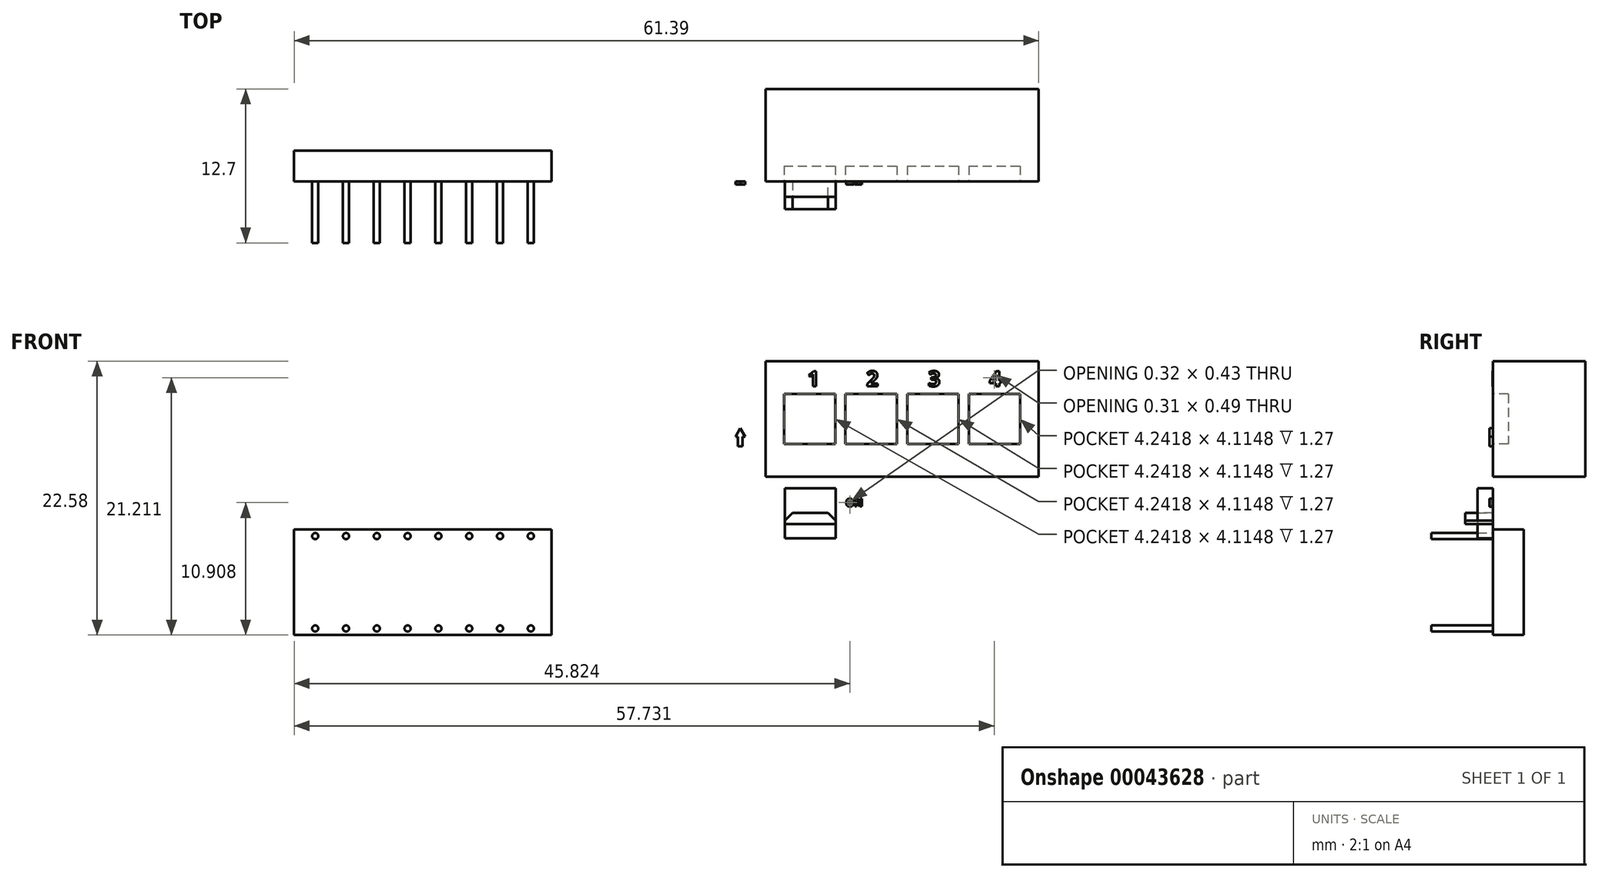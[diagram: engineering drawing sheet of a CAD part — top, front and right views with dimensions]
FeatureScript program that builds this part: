
annotation { "Feature Type Name" : "Feature", "Feature Type Description" : "" }
export const myFeature = defineFeature(function(context is Context, id is Id, definition is map)
    precondition{}
    {
        {
            var Q0;
            Q0=qCreatedBy(makeId("Front.planeOp"),FACE);
            var sketch = newSketch(context, id + "F0", { "sketchPlane" : qUnion([Q0])});
            skLineSegment(sketch, "E0.bottom", {"start": v(-10.98, 4.78) * mm, "end": v(11.55, 4.78) * mm});
            skLineSegment(sketch, "E0.top", {"start": v(-10.98, -4.77) * mm, "end": v(11.55, -4.77) * mm});
            skLineSegment(sketch, "E0.left", {"start": v(-10.98, 4.78) * mm, "end": v(-10.98, -4.77) * mm});
            skLineSegment(sketch, "E0.right", {"start": v(11.55, 4.78) * mm, "end": v(11.55, -4.77) * mm});
            skSolve(sketch);
        }
        {
            var Q0;
            Q0 = qSketchRegion(id + "F0", true);
            extrude(context, id + "F1", {"entities" : qUnion([Q0]), "oppositeDirection" : true, "depth" : 7.62 * mm});
        }
        {
            var Q0;
            Q0=qCreatedBy(makeId("Front.planeOp"),FACE);
            var sketch = newSketch(context, id + "F2", { "sketchPlane" : qUnion([Q0])});
            skLineSegment(sketch, "E1.bottom", {"start": v(-9.45, 2.07) * mm, "end": v(-5.21, 2.07) * mm});
            skLineSegment(sketch, "E1.top", {"start": v(-9.45, -2.05) * mm, "end": v(-5.21, -2.05) * mm});
            skLineSegment(sketch, "E1.left", {"start": v(-9.45, 2.07) * mm, "end": v(-9.45, -2.05) * mm});
            skLineSegment(sketch, "E1.right", {"start": v(-5.21, 2.07) * mm, "end": v(-5.21, -2.05) * mm});
            skLineSegment(sketch, "E2.bottom", {"start": v(-4.37, 2.07) * mm, "end": v(-0.13, 2.07) * mm});
            skLineSegment(sketch, "E2.left", {"start": v(-4.37, 2.07) * mm, "end": v(-4.37, -2.05) * mm});
            skLineSegment(sketch, "E2.top", {"start": v(-4.37, -2.05) * mm, "end": v(-0.13, -2.05) * mm});
            skLineSegment(sketch, "E2.right", {"start": v(-0.13, 2.07) * mm, "end": v(-0.13, -2.05) * mm});
            skLineSegment(sketch, "E3.bottom", {"start": v(0.7, 2.07) * mm, "end": v(4.95, 2.07) * mm});
            skLineSegment(sketch, "E3.left", {"start": v(0.7, 2.07) * mm, "end": v(0.7, -2.05) * mm});
            skLineSegment(sketch, "E3.top", {"start": v(0.7, -2.05) * mm, "end": v(4.95, -2.05) * mm});
            skLineSegment(sketch, "E3.right", {"start": v(4.95, 2.07) * mm, "end": v(4.95, -2.05) * mm});
            skLineSegment(sketch, "E4.bottom", {"start": v(5.79, 2.07) * mm, "end": v(10.03, 2.07) * mm});
            skLineSegment(sketch, "E4.left", {"start": v(5.79, 2.07) * mm, "end": v(5.79, -2.05) * mm});
            skLineSegment(sketch, "E4.top", {"start": v(5.79, -2.05) * mm, "end": v(10.03, -2.05) * mm});
            skLineSegment(sketch, "E4.right", {"start": v(10.03, 2.07) * mm, "end": v(10.03, -2.05) * mm});
            skSolve(sketch);
        }
        {
            var Q0;
            Q0 = qSketchRegion(id + "F2", true);
            extrude(context, id + "F3", {"entities" : qUnion([Q0]), "operationType" : NewBodyOperationType.REMOVE, "oppositeDirection" : true, "depth" : 1.27 * mm});
        }
        {
            var Q0;
            Q0=qCreatedBy(makeId("Front.planeOp"),FACE);
            var sketch = newSketch(context, id + "F4", { "sketchPlane" : qUnion([Q0])});
            skLineSegment(sketch, "E5.bottom", {"start": v(-9.38, -5.7) * mm, "end": v(-5.2, -5.7) * mm});
            skLineSegment(sketch, "E5.top", {"start": v(-9.38, -9.83) * mm, "end": v(-5.2, -9.83) * mm});
            skLineSegment(sketch, "E5.left", {"start": v(-9.38, -5.7) * mm, "end": v(-9.38, -9.83) * mm});
            skLineSegment(sketch, "E5.right", {"start": v(-5.2, -5.7) * mm, "end": v(-5.2, -9.83) * mm});
            skSolve(sketch);
        }
        {
            var Q0;
            Q0 = qSketchRegion(id + "F4", true);
            extrude(context, id + "F5", {"entities" : qUnion([Q0]), "depth" : 1.27 * mm});
        }
        {
            var Q0;
            Q0=qCreatedBy(makeId("Front.planeOp"),FACE);
            var sketch = newSketch(context, id + "F6", { "sketchPlane" : qUnion([Q0])});
            skLineSegment(sketch, "E6.bottom", {"start": v(-9.37, -8.66) * mm, "end": v(-5.19, -8.66) * mm});
            skLineSegment(sketch, "E6.top", {"start": v(-9.37, -7.72) * mm, "end": v(-5.19, -7.72) * mm});
            skLineSegment(sketch, "E6.left", {"start": v(-9.37, -8.66) * mm, "end": v(-9.37, -7.72) * mm});
            skLineSegment(sketch, "E6.right", {"start": v(-5.19, -8.66) * mm, "end": v(-5.19, -7.72) * mm});
            skSolve(sketch);
        }
        {
            var Q0;
            Q0 = qSketchRegion(id + "F6", true);
            var Q1;
            Q1=makeQuery(id+"F5.opExtrude","CAP_FACE",FACE,{"disambiguationData":[OSD([sQuery(id+"F4.wireOp",EDGE,"E5.bottom"),sQuery(id+"F4.wireOp",EDGE,"E5.top"),sQuery(id+"F4.wireOp",EDGE,"E5.left"),sQuery(id+"F4.wireOp",EDGE,"E5.right")])],"isStart":false});
            extrude(context, id + "F7", {"entities" : qUnion([Q0]), "endBoundEntityFace" : qUnion([Q1]), "depth" : 2.3 * mm});
        }
        {
            var Q0;
            Q0=makeQuery(id+"F7.opExtrude","SWEPT_EDGE",EDGE,{"disambiguationData":[OSD([sQuery(id+"F6.wireOp",EDGE,"E6.top"),sQuery(id+"F6.wireOp",EDGE,"E6.right")])]});
            var Q1;
            Q1=makeQuery(id+"F7.opExtrude","SWEPT_EDGE",EDGE,{"disambiguationData":[OSD([sQuery(id+"F6.wireOp",EDGE,"E6.top"),sQuery(id+"F6.wireOp",EDGE,"E6.left")])]});
            chamfer(context, id + "F8", {"entities" : qUnion([Q0, Q1]), "width" : 0.64 * mm, "tangentPropagation" : true});
        }
        {
            var Q0;
            Q0=qCreatedBy(makeId("Front.planeOp"),FACE);
            var sketch = newSketch(context, id + "F9", { "sketchPlane" : qUnion([Q0])});
            skLineSegment(sketch, "E7.bottom", {"start": v(-49.84, -9.12) * mm, "end": v(-28.63, -9.12) * mm});
            skLineSegment(sketch, "E7.top", {"start": v(-49.84, -17.8) * mm, "end": v(-28.63, -17.8) * mm});
            skLineSegment(sketch, "E7.left", {"start": v(-49.84, -9.12) * mm, "end": v(-49.84, -17.8) * mm});
            skLineSegment(sketch, "E7.right", {"start": v(-28.63, -9.12) * mm, "end": v(-28.63, -17.8) * mm});
            skLineSegment(sketch, "E8", {"start": v(-51.58, -5) * mm, "end": v(-30.05, -5) * mm, "construction": true});
            skLineSegment(sketch, "E9", {"start": v(-51.58, -22) * mm, "end": v(-28.39, -22) * mm, "construction": true});
            skSolve(sketch);
        }
        {
            var Q0;
            Q0 = qSketchRegion(id + "F9", true);
            extrude(context, id + "F10", {"entities" : qUnion([Q0]), "oppositeDirection" : true, "depth" : 2.54 * mm});
        }
        {
            var Q0;
            Q0=qCreatedBy(makeId("Front.planeOp"),FACE);
            var sketch = newSketch(context, id + "F11", { "sketchPlane" : qUnion([Q0])});
            skCircle(sketch, "E10", {"center": v(-32.86, -9.65) * mm, "radius": 0.25 * mm});
            skCircle(sketch, "E11", {"center": v(-35.4, -9.65) * mm, "radius": 0.25 * mm});
            skCircle(sketch, "E12", {"center": v(-37.95, -9.65) * mm, "radius": 0.25 * mm});
            skCircle(sketch, "E13", {"center": v(-40.49, -9.65) * mm, "radius": 0.25 * mm});
            skCircle(sketch, "E14", {"center": v(-43.03, -9.65) * mm, "radius": 0.25 * mm});
            skCircle(sketch, "E15", {"center": v(-45.57, -9.65) * mm, "radius": 0.25 * mm});
            skCircle(sketch, "E16", {"center": v(-48.1, -9.65) * mm, "radius": 0.25 * mm});
            skCircle(sketch, "E17", {"center": v(-48.1, -17.27) * mm, "radius": 0.25 * mm});
            skCircle(sketch, "E18", {"center": v(-45.57, -17.27) * mm, "radius": 0.25 * mm});
            skCircle(sketch, "E19", {"center": v(-43.03, -17.27) * mm, "radius": 0.25 * mm});
            skCircle(sketch, "E20", {"center": v(-40.49, -17.27) * mm, "radius": 0.25 * mm});
            skCircle(sketch, "E21", {"center": v(-37.95, -17.27) * mm, "radius": 0.25 * mm});
            skCircle(sketch, "E22", {"center": v(-35.4, -17.27) * mm, "radius": 0.25 * mm});
            skCircle(sketch, "E23", {"center": v(-32.87, -17.27) * mm, "radius": 0.25 * mm});
            skCircle(sketch, "E24", {"center": v(-30.33, -17.27) * mm, "radius": 0.25 * mm});
            skCircle(sketch, "E25", {"center": v(-30.33, -9.65) * mm, "radius": 0.25 * mm});
            skSolve(sketch);
        }
        {
            var Q0;
            Q0 = qSketchRegion(id + "F11", true);
            extrude(context, id + "F12", {"entities" : qUnion([Q0]), "depth" : 5.08 * mm});
        }
        {
            var Q0;
            Q0=qCreatedBy(makeId("Front.planeOp"),FACE);
            var sketch = newSketch(context, id + "F13", { "sketchPlane" : qUnion([Q0])});
            skText(sketch, "E26", { "text": "1", "fontName": "OpenSans-Bold.ttf"});
            skText(sketch, "E27", { "text": "2", "fontName": "OpenSans-Bold.ttf"});
            skText(sketch, "E28", { "text": "3", "fontName": "OpenSans-Bold.ttf"});
            skText(sketch, "E29", { "text": "4", "fontName": "OpenSans-Bold.ttf"});
            const initialGuessF13  = {"E26": [-0.00752, 0.0027, 1, 0, 0.00127], "E27": [-0.00266, 0.0027, 1, 0, 0.00127], "E28": [0.00243, 0.0027, 1, 0, 0.00127], "E29": [0.00747, 0.0027, 1, 0, 0.00127]};
            skSetInitialGuess(sketch, initialGuessF13);
            skSolve(sketch);
        }
        {
            var Q0;
            Q0 = qSketchRegion(id + "F13", true);
            extrude(context, id + "F14", {"entities" : qUnion([Q0]), "depth" : 0.03 * mm});
        }
        {
            var Q0;
            Q0=qCreatedBy(makeId("Front.planeOp"),FACE);
            var sketch = newSketch(context, id + "F15", { "sketchPlane" : qUnion([Q0])});
            skText(sketch, "E30", { "text": "ON", "fontName": "OpenSans-Bold.ttf"});
            const initialGuessF15  = {"E30": [-0.00437, -0.00721, 1, 0, 0.00064]};
            skSetInitialGuess(sketch, initialGuessF15);
            skSolve(sketch);
        }
        {
            var Q0;
            Q0 = qSketchRegion(id + "F15", true);
            extrude(context, id + "F16", {"entities" : qUnion([Q0]), "depth" : 0.28 * mm});
        }
        {
            var Q0;
            Q0=qCreatedBy(makeId("Front.planeOp"),FACE);
            var sketch = newSketch(context, id + "F17", { "sketchPlane" : qUnion([Q0])});
            skLineSegment(sketch, "E31", {"start": v(-13.04, -0.76) * mm, "end": v(-13.44, -1.44) * mm});
            skLineSegment(sketch, "E32", {"start": v(-13.04, -0.76) * mm, "end": v(-12.65, -1.44) * mm});
            skLineSegment(sketch, "E33", {"start": v(-12.65, -1.44) * mm, "end": v(-13.44, -1.44) * mm});
            skLineSegment(sketch, "E34.bottom", {"start": v(-13.24, -1.44) * mm, "end": v(-12.85, -1.44) * mm});
            skLineSegment(sketch, "E34.top", {"start": v(-13.24, -2.23) * mm, "end": v(-12.85, -2.23) * mm});
            skLineSegment(sketch, "E34.left", {"start": v(-13.24, -1.44) * mm, "end": v(-13.24, -2.23) * mm});
            skLineSegment(sketch, "E34.right", {"start": v(-12.85, -1.44) * mm, "end": v(-12.85, -2.23) * mm});
            skSolve(sketch);
        }
        {
            var Q0;
            Q0 = qSketchRegion(id + "F17", true);
            extrude(context, id + "F18", {"entities" : qUnion([Q0]), "depth" : 0.28 * mm});
        }
    });
